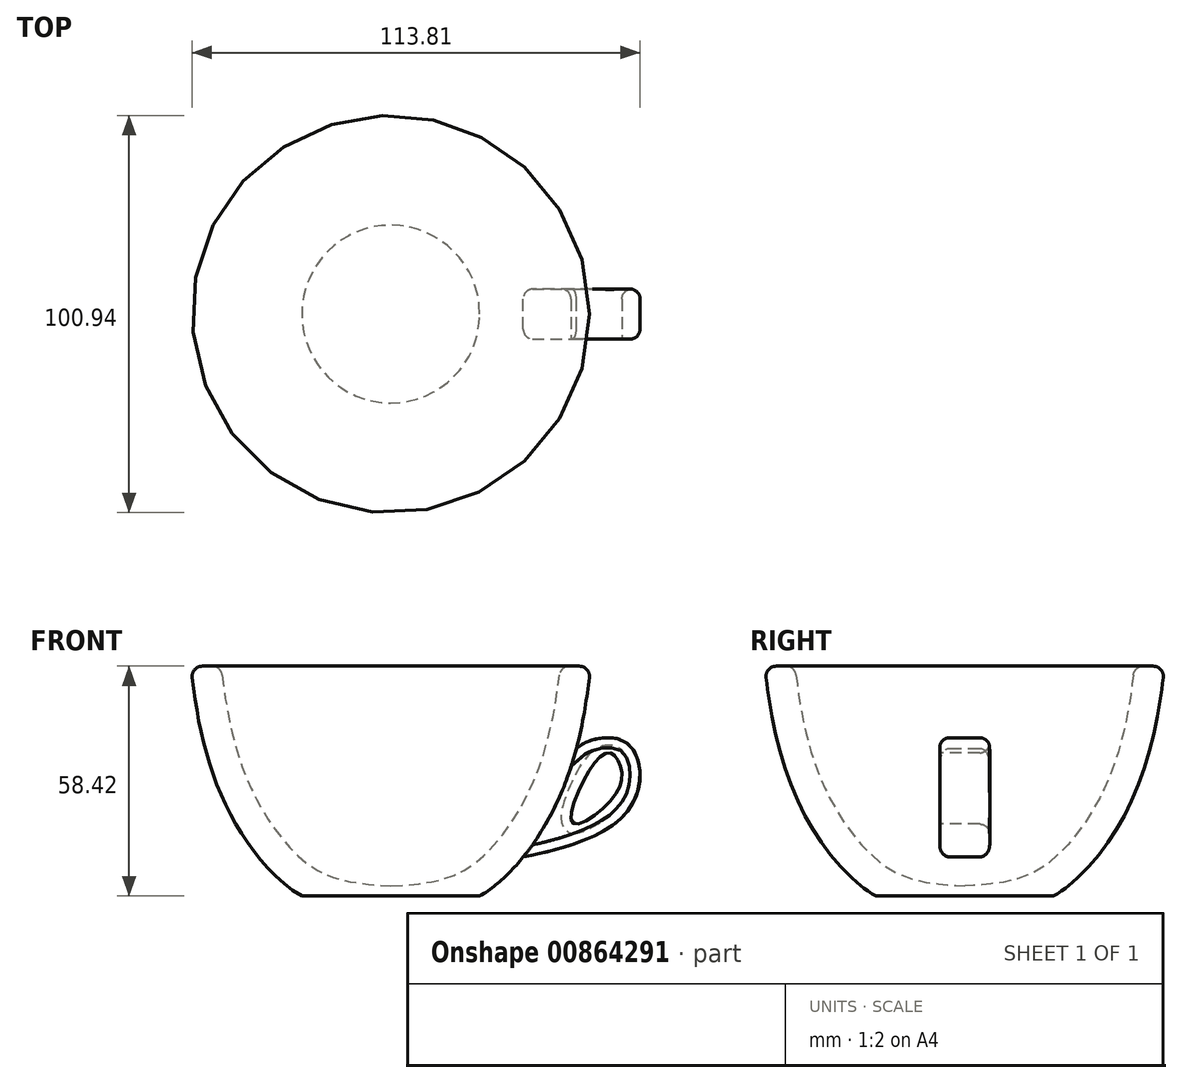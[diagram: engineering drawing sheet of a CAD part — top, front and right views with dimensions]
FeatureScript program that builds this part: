
annotation { "Feature Type Name" : "Feature", "Feature Type Description" : "" }
export const myFeature = defineFeature(function(context is Context, id is Id, definition is map)
    precondition{}
    {
        {
            var Q0;
            Q0=qCreatedBy(makeId("Top.planeOp"),FACE);
            cPlane(context, id + "F0", {"entities" : qUnion([Q0]), "cplaneType" : CPlaneType.OFFSET, "offset" : 63.5 * mm, "width" : 152.4 * mm, "height" : 152.4 * mm});
        }
        {
            var Q0;
            Q0=qCreatedBy(makeId("Front.planeOp"),FACE);
            var sketch = newSketch(context, id + "F1", { "sketchPlane" : qUnion([Q0])});
            skFitSpline(sketch, "E0", {"points": [v(0, 0) * mm, v(22.63, 5.1) * mm, v(41.68, 27.74) * mm, v(48.86, 50.1) * mm, v(50.8, 63.5) * mm], "startDerivative": vector(92.73, 6.08) * mm, "endDerivative": vector(8.5, 70.77) * mm});
            skLineSegment(sketch, "E1", {"start": v(0, 63.5) * mm, "end": v(0, 0) * mm});
            skLineSegment(sketch, "E2", {"start": v(50.8, 63.5) * mm, "end": v(0, 63.5) * mm});
            skSolve(sketch);
        }
        {
            var Q0;
            Q0 = qSketchRegion(id + "F1", true);
            var Q1;
            Q1=sQuery(id+"F1.wireOp",EDGE,"E1");
            revolve(context, id + "F2", {"surfaceOperationType" : NewSurfaceOperationType.NEW, "entities" : qUnion([Q0]), "axis" : qUnion([Q1]), "revolveType" : RevolveType.FULL});
        }
        {
            var Q0;
            Q0=makeQuery(id+"F2.opRevolve","SWEPT_FACE",FACE,{"disambiguationData":[OSD([sQuery(id+"F1.wireOp",EDGE,"E2")])]});
            shell(context, id + "F3", {"entities" : qUnion([Q0]), "thickness" : 7.62 * mm});
        }
        {
            var Q0;
            Q0=qCreatedBy(makeId("Front.planeOp"),FACE);
            var sketch = newSketch(context, id + "F4", { "sketchPlane" : qUnion([Q0])});
            skFitSpline(sketch, "E3", {"points": [v(33.65, 15.02) * mm, v(56.3, 23.03) * mm, v(63.3, 34.89) * mm, v(59, 44.58) * mm, v(47.17, 42.67) * mm], "startDerivative": vector(64.14, 12.19) * mm, "endDerivative": vector(-33.45, -29.97) * mm});
            skFitSpline(sketch, "E4", {"points": [v(0, 0) * mm, v(22.63, 5.1) * mm, v(41.68, 27.74) * mm, v(48.86, 50.1) * mm, v(50.8, 63.5) * mm], "startDerivative": vector(92.73, 6.08) * mm, "endDerivative": vector(8.5, 70.77) * mm});
            skSolve(sketch);
        }
        {
            var Q0;
            Q0 = qSketchRegion(id + "F4", true);
            extrude(context, id + "F5", {"entities" : qUnion([Q0]), "operationType" : NewBodyOperationType.ADD, "endBound" : BoundingType.SYMMETRIC, "depth" : 12.7 * mm, "offsetDistance" : 25.4 * mm});
        }
        {
            var Q0;
            Q0=makeQuery(id+"F5.opExtrude","CAP_FACE",FACE,{"disambiguationData":[OSD([sQuery(id+"F4.wireOp",EDGE,"E3"),sQuery(id+"F4.wireOp",EDGE,"E4")])],"isStart":false});
            var sketch = newSketch(context, id + "F6", { "sketchPlane" : qUnion([Q0])});
            skFitSpline(sketch, "E5", {"points": [v(55.77, 41.45) * mm, v(58.57, 37.29) * mm, v(56.03, 29.5) * mm, v(46.34, 23.57) * mm, v(49.84, 35.96) * mm, v(55.77, 41.45) * mm]});
            skSolve(sketch);
        }
        {
            var Q0;
            Q0=makeQuery(id+"F6.imprint","IMPRINT",FACE,{"disambiguationData":[TD([[makeQuery(id+"F6.imprint","IMPRINT",EDGE,{"derivedFrom":sQuery(id+"F6.wireOp",EDGE,"E5")}),-1.0]])]});
            extrude(context, id + "F7", {"entities" : qUnion([Q0]), "operationType" : NewBodyOperationType.REMOVE, "endBound" : BoundingType.THROUGH_ALL, "oppositeDirection" : true, "depth" : 25.4 * mm, "offsetDistance" : 25.4 * mm});
        }
        {
            var Q0;
            Q0=makeQuery(id+"F7.boolean.opBoolean","INTERSECT",EDGE,{"derivedFrom":[makeQuery(id+"F5.opExtrude","CAP_FACE",FACE,{"disambiguationData":[OSD([sQuery(id+"F4.wireOp",EDGE,"E3"),sQuery(id+"F4.wireOp",EDGE,"E4")])],"isStart":true}),makeQuery(id+"F7.opExtrude","SWEPT_FACE",FACE,{"disambiguationData":[OSD([sQuery(id+"F6.wireOp",EDGE,"E5")])]})]});
            var Q1;
            Q1=makeQuery(id+"F5.opExtrude","CAP_EDGE",EDGE,{"disambiguationData":[OSD([sQuery(id+"F4.wireOp",EDGE,"E3")])],"isStart":true});
            var Q2;
            Q2=makeQuery(id+"F5.opExtrude","CAP_EDGE",EDGE,{"disambiguationData":[OSD([sQuery(id+"F4.wireOp",EDGE,"E3")])],"isStart":false});
            var Q3;
            Q3=makeQuery(id+"F7.boolean.opBoolean","COPY",EDGE,{"derivedFrom":makeQuery(id+"F7.opExtrude","CAP_EDGE",EDGE,{"disambiguationData":[OSD([sQuery(id+"F6.wireOp",EDGE,"E5")])],"isStart":true})});
            fillet(context, id + "F8", {"entities" : qUnion([Q0, Q1, Q2, Q3]), "radius" : 2.54 * mm, "tangentPropagation" : true, "allowEdgeOverflow" : false});
        }
        {
            var Q0;
            Q0=makeQuery(id+"F2.opRevolve","SWEPT_EDGE",EDGE,{"disambiguationData":[OSD([sQuery(id+"F1.wireOp",EDGE,"E0"),sQuery(id+"F1.wireOp",EDGE,"E2")])]});
            var Q1;
            Q1=makeQuery(id+"F3.opShell","OFFSET_EDGE",EDGE,{"disambiguationData":[OSD([sQuery(id+"F1.wireOp",EDGE,"E0"),sQuery(id+"F1.wireOp",EDGE,"E2")])]});
            fillet(context, id + "F9", {"entities" : qUnion([Q0, Q1]), "radius" : 2.54 * mm, "tangentPropagation" : true, "allowEdgeOverflow" : false});
        }
        {
            var Q0;
            Q0=qCreatedBy(makeId("Top.planeOp"),FACE);
            var sketch = newSketch(context, id + "F10", { "sketchPlane" : qUnion([Q0])});
            skCircle(sketch, "E6", {"center": v(0, 0) * mm, "radius": 31.29 * mm});
            skSolve(sketch);
        }
        {
            var Q0;
            Q0=makeQuery(id+"F10.imprint","IMPRINT",FACE,{"disambiguationData":[TD([[makeQuery(id+"F10.imprint","IMPRINT",EDGE,{"derivedFrom":sQuery(id+"F10.wireOp",EDGE,"E6")}),1.0]])]});
            extrude(context, id + "F11", {"entities" : qUnion([Q0]), "operationType" : NewBodyOperationType.REMOVE, "depth" : 5.08 * mm, "offsetDistance" : 25.4 * mm});
        }
    });
